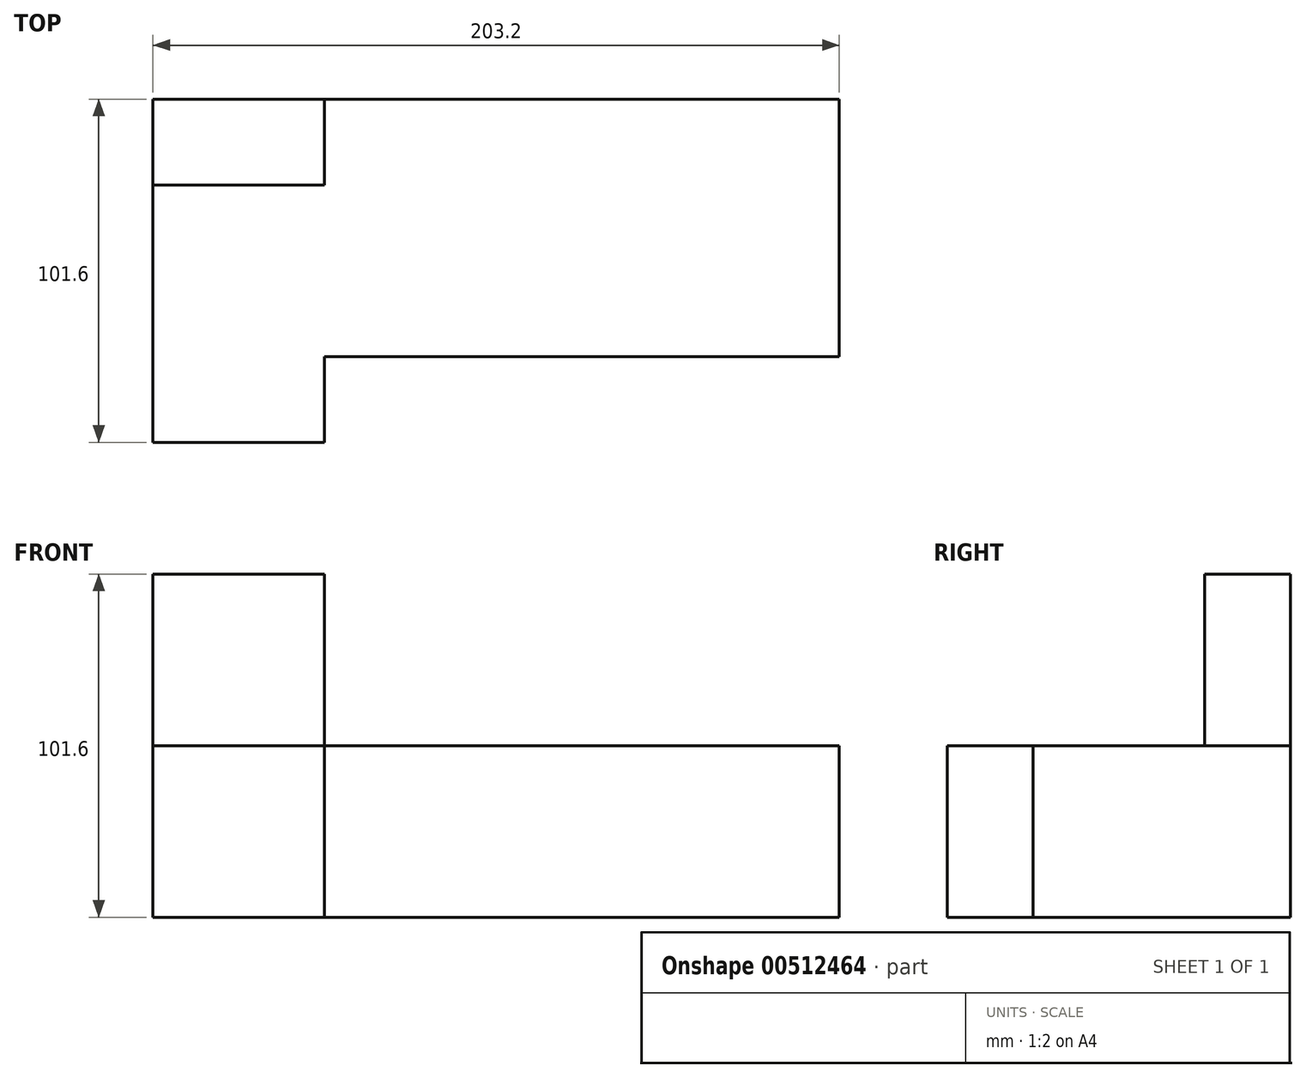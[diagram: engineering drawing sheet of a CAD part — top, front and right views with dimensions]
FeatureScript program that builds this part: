
annotation { "Feature Type Name" : "Feature", "Feature Type Description" : "" }
export const myFeature = defineFeature(function(context is Context, id is Id, definition is map)
    precondition{}
    {
        {
            var Q0;
            Q0=qCreatedBy(makeId("Front.planeOp"),FACE);
            var sketch = newSketch(context, id + "F0", { "sketchPlane" : qUnion([Q0])});
            skLineSegment(sketch, "E0.bottom", {"start": v(0, 0) * mm, "end": v(203.2, 0) * mm});
            skLineSegment(sketch, "E0.top", {"start": v(0, 50.8) * mm, "end": v(203.2, 50.8) * mm});
            skLineSegment(sketch, "E0.left", {"start": v(0, 0) * mm, "end": v(0, 50.8) * mm});
            skLineSegment(sketch, "E0.right", {"start": v(203.2, 0) * mm, "end": v(203.2, 50.8) * mm});
            skSolve(sketch);
        }
        {
            var Q0;
            Q0=makeQuery(id+"F0.imprint","IMPRINT",FACE,{"disambiguationData":[TD([[makeQuery(id+"F0.imprint","IMPRINT",EDGE,{"derivedFrom":sQuery(id+"F0.wireOp",EDGE,"E0.bottom")}),1.0]])]});
            extrude(context, id + "F1", {"entities" : qUnion([Q0]), "depth" : 101.6 * mm});
        }
        {
            var Q0;
            Q0=makeQuery(id+"F1.opExtrude","CAP_FACE",FACE,{"disambiguationData":[OSD([sQuery(id+"F0.wireOp",EDGE,"E0.bottom"),sQuery(id+"F0.wireOp",EDGE,"E0.top"),sQuery(id+"F0.wireOp",EDGE,"E0.left"),sQuery(id+"F0.wireOp",EDGE,"E0.right")])],"isStart":false});
            var sketch = newSketch(context, id + "F2", { "sketchPlane" : qUnion([Q0])});
            skLineSegment(sketch, "E1.bottom", {"start": v(203.2, 0) * mm, "end": v(50.8, 0) * mm});
            skLineSegment(sketch, "E1.top", {"start": v(203.2, 50.8) * mm, "end": v(50.8, 50.8) * mm});
            skLineSegment(sketch, "E1.left", {"start": v(203.2, 0) * mm, "end": v(203.2, 50.8) * mm});
            skLineSegment(sketch, "E1.right", {"start": v(50.8, 0) * mm, "end": v(50.8, 50.8) * mm});
            skSolve(sketch);
        }
        {
            var Q0;
            Q0=makeQuery(id+"F2.imprint","IMPRINT",FACE,{"disambiguationData":[TD([[makeQuery(id+"F2.imprint","IMPRINT",EDGE,{"derivedFrom":sQuery(id+"F2.wireOp",EDGE,"E1.bottom")}),1.0]])]});
            extrude(context, id + "F3", {"entities" : qUnion([Q0]), "operationType" : NewBodyOperationType.REMOVE, "oppositeDirection" : true, "depth" : 25.4 * mm});
        }
        {
            var Q0;
            Q0=makeQuery(id+"F1.opExtrude","SWEPT_FACE",FACE,{"disambiguationData":[OSD([sQuery(id+"F0.wireOp",EDGE,"E0.top")])]});
            var sketch = newSketch(context, id + "F4", { "sketchPlane" : qUnion([Q0])});
            skLineSegment(sketch, "E2.bottom", {"start": v(0, 0) * mm, "end": v(50.8, 0) * mm});
            skLineSegment(sketch, "E2.top", {"start": v(0, -25.4) * mm, "end": v(50.8, -25.4) * mm});
            skLineSegment(sketch, "E2.left", {"start": v(0, 0) * mm, "end": v(0, -25.4) * mm});
            skLineSegment(sketch, "E2.right", {"start": v(50.8, 0) * mm, "end": v(50.8, -25.4) * mm});
            skSolve(sketch);
        }
        {
            var Q0;
            Q0=makeQuery(id+"F4.imprint","IMPRINT",FACE,{"disambiguationData":[TD([[makeQuery(id+"F4.imprint","IMPRINT",EDGE,{"derivedFrom":sQuery(id+"F4.wireOp",EDGE,"E2.bottom")}),-1.0]])]});
            extrude(context, id + "F5", {"entities" : qUnion([Q0]), "operationType" : NewBodyOperationType.ADD, "depth" : 50.8 * mm});
        }
    });
